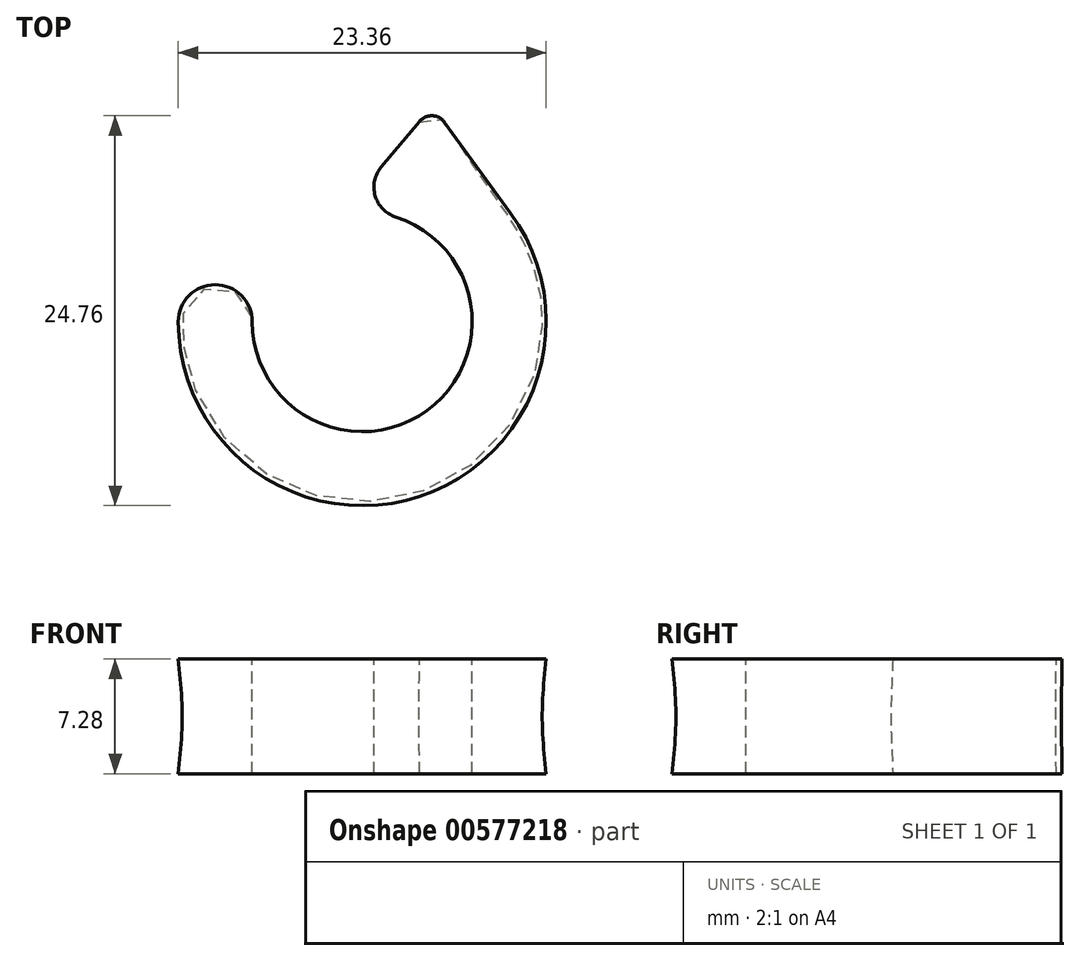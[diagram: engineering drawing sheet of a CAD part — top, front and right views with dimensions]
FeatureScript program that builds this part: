
annotation { "Feature Type Name" : "Feature", "Feature Type Description" : "" }
export const myFeature = defineFeature(function(context is Context, id is Id, definition is map)
    precondition{}
    {
        {
            var Q0;
            Q0=qCreatedBy(makeId("Top.planeOp"),FACE);
            var sketch = newSketch(context, id + "F0", { "sketchPlane" : qUnion([Q0])});
            skPoint(sketch, "E0", {"position": v(-11.43, 0) * mm});
            skLineSegment(sketch, "E1", {"start": v(9.2, 6.79) * mm, "end": v(5.23, 12.6) * mm});
            skLineSegment(sketch, "E2", {"start": v(1.21, 9.83) * mm, "end": v(3.61, 12.69) * mm});
            skArc(sketch, "E3", {"start": v(1.21, 9.83) * mm, "mid": v(0.82, 8) * mm, "end": v(2.13, 6.65) * mm});
            skArc(sketch, "E4", {"start": v(-11.43, 0) * mm, "mid": v(3.57, -10.86) * mm, "end": v(9.2, 6.79) * mm});
            skPoint(sketch, "E5", {"position": v(-6.99, 0) * mm});
            skArc(sketch, "E6", {"start": v(-6.99, 0) * mm, "mid": v(4.12, -5.64) * mm, "end": v(2.13, 6.65) * mm});
            skArc(sketch, "E7", {"start": v(-6.99, 0) * mm, "mid": v(-9.2, 2.22) * mm, "end": v(-11.43, 0) * mm});
            skPoint(sketch, "E8.visualSharp", {"position": v(4.48, 13.72) * mm});
            skArc(sketch, "E8.filletArc", {"start": v(5.23, 12.6) * mm, "mid": v(4.44, 13.05) * mm, "end": v(3.61, 12.69) * mm});
            skSolve(sketch);
        }
        {
            var Q0;
            Q0=makeQuery(id+"F0.imprint","IMPRINT",FACE,{"disambiguationData":[TD([[makeQuery(id+"F0.imprint","IMPRINT",EDGE,{"derivedFrom":sQuery(id+"F0.wireOp",EDGE,"E1")}),1.0]])]});
            cPlane(context, id + "F1", {"entities" : qUnion([Q0]), "cplaneType" : CPlaneType.OFFSET, "offset" : 3.64 * mm, "width" : 152.4 * mm, "height" : 152.4 * mm});
        }
        {
            var Q0;
            Q0=qCreatedBy(id+"F1.planeOp",FACE);
            var sketch = newSketch(context, id + "F2", { "sketchPlane" : qUnion([Q0])});
            skPoint(sketch, "E9", {"position": v(-11.68, 0) * mm});
            skLineSegment(sketch, "E10", {"start": v(9.4, 6.94) * mm, "end": v(5.24, 12.66) * mm});
            skLineSegment(sketch, "E11", {"start": v(1.21, 9.83) * mm, "end": v(3.64, 12.72) * mm});
            skArc(sketch, "E12", {"start": v(1.21, 9.83) * mm, "mid": v(0.82, 8) * mm, "end": v(2.13, 6.65) * mm});
            skArc(sketch, "E13", {"start": v(-11.68, 0) * mm, "mid": v(3.65, -11.1) * mm, "end": v(9.4, 6.94) * mm});
            skPoint(sketch, "E14", {"position": v(-6.99, 0) * mm});
            skArc(sketch, "E15", {"start": v(-6.99, 0) * mm, "mid": v(4.12, -5.64) * mm, "end": v(2.13, 6.65) * mm});
            skArc(sketch, "E16", {"start": v(-6.99, 0) * mm, "mid": v(-9.33, 2.35) * mm, "end": v(-11.68, 0) * mm});
            skPoint(sketch, "E17.visualSharp", {"position": v(4.48, 13.72) * mm});
            skArc(sketch, "E17.filletArc", {"start": v(5.24, 12.66) * mm, "mid": v(4.45, 13.08) * mm, "end": v(3.64, 12.72) * mm});
            skSolve(sketch);
        }
        {
            var Q0;
            Q0=makeQuery(id+"F0.imprint","IMPRINT",FACE,{"disambiguationData":[TD([[makeQuery(id+"F0.imprint","IMPRINT",EDGE,{"derivedFrom":sQuery(id+"F0.wireOp",EDGE,"E1")}),1.0]])]});
            cPlane(context, id + "F3", {"entities" : qUnion([Q0]), "cplaneType" : CPlaneType.OFFSET, "offset" : 3.64 * mm, "oppositeDirection" : true, "width" : 152.4 * mm, "height" : 152.4 * mm});
        }
        {
            var Q0;
            Q0=qCreatedBy(id+"F3.planeOp",FACE);
            var sketch = newSketch(context, id + "F4", { "sketchPlane" : qUnion([Q0])});
            skPoint(sketch, "E18", {"position": v(-11.68, 0) * mm});
            skLineSegment(sketch, "E19", {"start": v(9.4, 6.94) * mm, "end": v(5.24, 12.66) * mm});
            skLineSegment(sketch, "E20", {"start": v(1.21, 9.83) * mm, "end": v(3.64, 12.72) * mm});
            skArc(sketch, "E21", {"start": v(1.21, 9.83) * mm, "mid": v(0.82, 8) * mm, "end": v(2.13, 6.65) * mm});
            skArc(sketch, "E22", {"start": v(-11.68, 0) * mm, "mid": v(3.65, -11.1) * mm, "end": v(9.4, 6.94) * mm});
            skPoint(sketch, "E23", {"position": v(-6.99, 0) * mm});
            skArc(sketch, "E24", {"start": v(-6.99, 0) * mm, "mid": v(4.12, -5.64) * mm, "end": v(2.13, 6.65) * mm});
            skArc(sketch, "E25", {"start": v(-6.99, 0) * mm, "mid": v(-9.33, 2.35) * mm, "end": v(-11.68, 0) * mm});
            skPoint(sketch, "E26.visualSharp", {"position": v(4.48, 13.72) * mm});
            skArc(sketch, "E26.filletArc", {"start": v(5.24, 12.66) * mm, "mid": v(4.45, 13.08) * mm, "end": v(3.64, 12.72) * mm});
            skSolve(sketch);
        }
        {
            var Q0;
            Q0=makeQuery(id+"F4.imprint","IMPRINT",FACE,{"disambiguationData":[TD([[makeQuery(id+"F4.imprint","IMPRINT",EDGE,{"derivedFrom":sQuery(id+"F4.wireOp",EDGE,"E19")}),1.0]])]});
            var Q1;
            Q1=makeQuery(id+"F0.imprint","IMPRINT",FACE,{"disambiguationData":[TD([[makeQuery(id+"F0.imprint","IMPRINT",EDGE,{"derivedFrom":sQuery(id+"F0.wireOp",EDGE,"E1")}),1.0]])]});
            var Q2;
            Q2=makeQuery(id+"F2.imprint","IMPRINT",FACE,{"disambiguationData":[TD([[makeQuery(id+"F2.imprint","IMPRINT",EDGE,{"derivedFrom":sQuery(id+"F2.wireOp",EDGE,"E10")}),1.0]])]});
            loft(context, id + "F5", {"sheetProfilesArray" : [{ "sheetProfileEntities" : qUnion([Q0]) }, { "sheetProfileEntities" : qUnion([Q1]) }, { "sheetProfileEntities" : qUnion([Q2]) }]});
        }
    });
